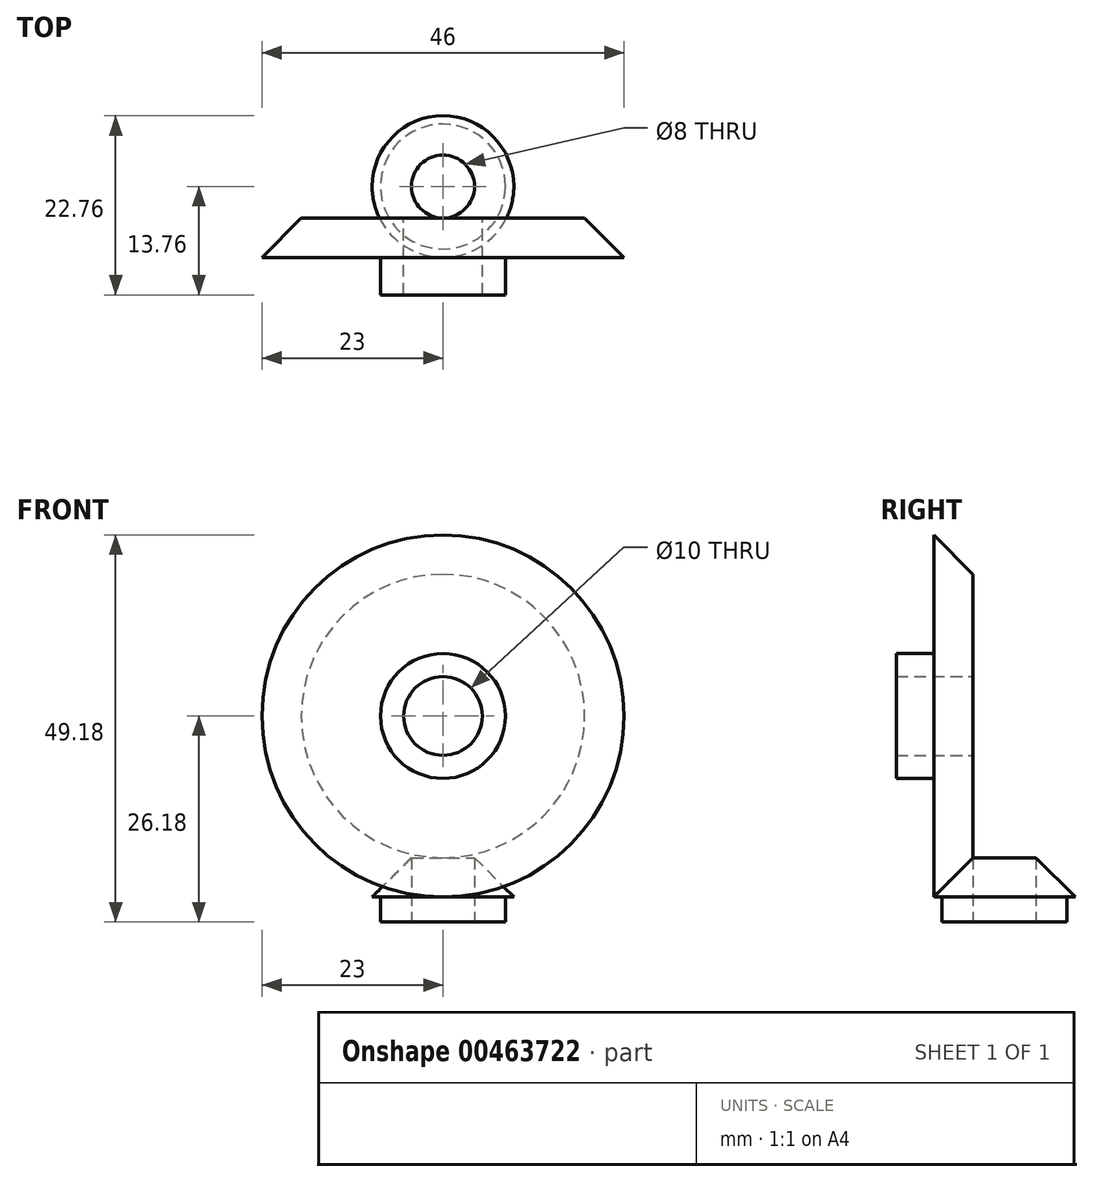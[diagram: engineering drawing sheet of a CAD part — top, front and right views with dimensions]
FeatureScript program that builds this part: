
annotation { "Feature Type Name" : "Feature", "Feature Type Description" : "" }
export const myFeature = defineFeature(function(context is Context, id is Id, definition is map)
    precondition{}
    {
        {
            var Q0;
            Q0=qCreatedBy(makeId("Right.planeOp"),FACE);
            var sketch = newSketch(context, id + "F0", { "sketchPlane" : qUnion([Q0])});
            skLineSegment(sketch, "E0", {"start": v(-9, 0) * mm, "end": v(-1.38, 0) * mm});
            skLineSegment(sketch, "E1", {"start": v(-1.38, 0) * mm, "end": v(-1.38, -15.38) * mm});
            skLineSegment(sketch, "E2", {"start": v(-1.38, -15.38) * mm, "end": v(-9, -23) * mm});
            skLineSegment(sketch, "E3", {"start": v(-9, -23) * mm, "end": v(-9, 0) * mm});
            skLineSegment(sketch, "E4", {"start": v(-1.38, -15.38) * mm, "end": v(0, -15.38) * mm});
            skLineSegment(sketch, "E5", {"start": v(0, -15.38) * mm, "end": v(0, -23) * mm});
            skLineSegment(sketch, "E6", {"start": v(0, -23) * mm, "end": v(-9, -23) * mm});
            skSolve(sketch);
        }
        {
            var Q0;
            Q0=makeQuery(id+"F0.imprint","IMPRINT",FACE,{"disambiguationData":[TD([[makeQuery(id+"F0.imprint","IMPRINT",EDGE,{"derivedFrom":sQuery(id+"F0.wireOp",EDGE,"E0")}),-1.0]])]});
            var Q1;
            Q1=sQuery(id+"F0.wireOp",EDGE,"E0");
            revolve(context, id + "F1", {"entities" : qUnion([Q0]), "axis" : qUnion([Q1]), "revolveType" : RevolveType.FULL});
        }
        {
            var Q0;
            Q0=makeQuery(id+"F0.imprint","IMPRINT",FACE,{"disambiguationData":[TD([[makeQuery(id+"F0.imprint","IMPRINT",EDGE,{"derivedFrom":sQuery(id+"F0.wireOp",EDGE,"E2")}),1.0]])]});
            var Q1;
            Q1=sQuery(id+"F0.wireOp",EDGE,"E5");
            revolve(context, id + "F2", {"entities" : qUnion([Q0]), "axis" : qUnion([Q1]), "revolveType" : RevolveType.FULL});
        }
        {
            var Q0;
            Q0=makeQuery(id+"F1.opRevolve","SWEPT_FACE",FACE,{"disambiguationData":[OSD([sQuery(id+"F0.wireOp",EDGE,"E1")])]});
            var sketch = newSketch(context, id + "F3", { "sketchPlane" : qUnion([Q0])});
            skCircle(sketch, "E7", {"center": v(0, 0) * mm, "radius": 5 * mm});
            skSolve(sketch);
        }
        {
            var Q0;
            Q0 = qSketchRegion(id + "F3", true);
            extrude(context, id + "F4", {"entities" : qUnion([Q0]), "operationType" : NewBodyOperationType.REMOVE, "endBound" : BoundingType.THROUGH_ALL, "oppositeDirection" : true, "depth" : 25.4 * mm});
        }
        {
            var Q0;
            Q0=makeQuery(id+"F2.opRevolve","SWEPT_FACE",FACE,{"disambiguationData":[OSD([sQuery(id+"F0.wireOp",EDGE,"E6")])]});
            var sketch = newSketch(context, id + "F5", { "sketchPlane" : qUnion([Q0])});
            skCircle(sketch, "E8", {"center": v(0, 0) * mm, "radius": 4 * mm});
            skSolve(sketch);
        }
        {
            var Q0;
            Q0 = qSketchRegion(id + "F5", true);
            extrude(context, id + "F6", {"entities" : qUnion([Q0]), "operationType" : NewBodyOperationType.REMOVE, "endBound" : BoundingType.THROUGH_ALL, "oppositeDirection" : true, "depth" : 25.4 * mm});
        }
        {
            var Q0;
            Q0=qCreatedBy(makeId("Right.planeOp"),FACE);
            var sketch = newSketch(context, id + "F7", { "sketchPlane" : qUnion([Q0])});
            skLineSegment(sketch, "E9.bottom", {"start": v(4, -18) * mm, "end": v(-4, -18) * mm});
            skLineSegment(sketch, "E9.top", {"start": v(4, 18) * mm, "end": v(-4, 18) * mm});
            skLineSegment(sketch, "E9.left", {"start": v(4, -18) * mm, "end": v(4, 18) * mm});
            skLineSegment(sketch, "E9.right", {"start": v(-4, -18) * mm, "end": v(-4, 18) * mm});
            skPoint(sketch, "E9.middle", {"position": v(0, 0) * mm});
            skLineSegment(sketch, "E10.1", {"start": v(-4, -18) * mm, "end": v(4, -18) * mm, "construction": true});
            skSolve(sketch);
        }
        {
            var Q0;
            Q0 = qSketchRegion(id + "F7", true);
            extrude(context, id + "F8", {"entities" : qUnion([Q0]), "operationType" : NewBodyOperationType.REMOVE, "endBound" : BoundingType.THROUGH_ALL, "oppositeDirection" : true, "depth" : 25.4 * mm, "hasSecondDirection" : true, "secondDirectionBound" : SecondDirectionBoundingType.THROUGH_ALL, "secondDirectionOppositeDirection" : false, "secondDirectionDepth" : 25.4 * mm});
        }
        {
            var Q0;
            Q0=makeQuery(id+"F2.opRevolve","SWEPT_FACE",FACE,{"disambiguationData":[OSD([sQuery(id+"F0.wireOp",EDGE,"E6")])]});
            var sketch = newSketch(context, id + "F9", { "sketchPlane" : qUnion([Q0])});
            skCircle(sketch, "E11", {"center": v(0, 0) * mm, "radius": 7.94 * mm});
            skCircle(sketch, "E12.0", {"center": v(0, 0) * mm, "radius": 4 * mm});
            skSolve(sketch);
        }
        {
            var Q0;
            Q0 = qSketchRegion(id + "F9", true);
            extrude(context, id + "F10", {"entities" : qUnion([Q0]), "operationType" : NewBodyOperationType.ADD, "depth" : 3.17 * mm});
        }
        {
            var Q0;
            Q0=makeQuery(id+"F1.opRevolve","SWEPT_FACE",FACE,{"disambiguationData":[OSD([sQuery(id+"F0.wireOp",EDGE,"E3")])]});
            var sketch = newSketch(context, id + "F11", { "sketchPlane" : qUnion([Q0])});
            skCircle(sketch, "E13", {"center": v(0, 0) * mm, "radius": 7.94 * mm});
            skCircle(sketch, "E14.0", {"center": v(0, 0) * mm, "radius": 5 * mm});
            skSolve(sketch);
        }
        {
            var Q0;
            Q0 = qSketchRegion(id + "F11", true);
            extrude(context, id + "F12", {"entities" : qUnion([Q0]), "operationType" : NewBodyOperationType.ADD, "depth" : 4.76 * mm});
        }
    });
